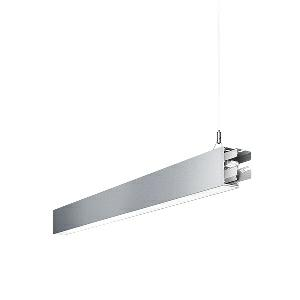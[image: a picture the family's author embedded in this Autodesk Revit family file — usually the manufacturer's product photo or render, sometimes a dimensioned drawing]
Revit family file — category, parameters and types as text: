
# Revit family: idoo_line_-_ilp_4000_vtl_d_mid_00806470_1443
name_source: partatom
category: Lighting Fixtures
units: mm (PartAtom-declared; Revit-internal decimal feet)

## family parameters
Cut with Voids When Loaded = No
Host = Face
Light Source = No
Part Type = Normal
Room Calculation Point = No
Round Connector Dimension = Use Diameter
Shared = No

## types (1)
- IDOO.line - ILP 4000/VTL/D MID (1 x LED, 3850 lm, 2700-6500K)
    Apparent Load = 39 VA
    Approval mark = CE
    CIE Flux Codes = 66 91 98 40 100
    Color Rendering = 90-100
    Color Temperature = 2700-6500K
    Control Gear = Electronic ballast
    Default Elevation = 1800 mm
    Description = ILP 4000/VTL/D|Suspended luminaire|light source: LED|connected load: 220-240 V, 50/60 Hz|Power consumption: approx. 39 W|standby: approx. 0,25|luminous flux: 3850 lm|luminous efficacy: 98 lm/W|light distribution: Direct/indirect|direct ratio: approx. 40 %|colour temperature: Cold white, ca. 2700-6500 K|color rendering index (CRI): >= 90|chromaticity tolerance:  3 SDCM|System of protection: IP 40|technology: Continuously dimmable|luminaire body|material: Sectional aluminium|colour: Silver|lamp cover: Acrylic (PMMA), Clear|mains lead: 1,0 m With free stranded wires|Fastening: Steel cable 0.3 - 0.7 m|glare control: Prism aperture|luminance(L65): <= 2700 cd/m|unified glare rating(4H 8H): <=  16|special features: Specified values at approx. 4000 K, DALI Load 1x, Through-wired, up to 18 m on one mains connection, External control required for Dali Device type 8, Flicker-free, Constant luminous flux between 2700 and 6500 K, Constant colour temperature over the whole dimming range, Suitable as emergency lighting, Mechanical and electrical connection of the individual modules without tools|
    Frequency = 50 Hz
    Height = 110 mm
    Lamp = 1 x LED
    Lamp Light Flux = 3850 lm
    Lamp count = 1
    Length = 1402 mm
    Luminous efficacy = 99 lm/W
    Manufacturer = Waldmann
    ModVariant = No
    Model = 00806470
    Mounting Place = Ceiling
    Mounting Type = Pendant
    Number of Poles = 1
    OnlyDefault = Yes
    Power Factor = 1
    Product Name = IDOO.line - ILP 4000/VTL/D MID
    Product group = Suspended luminaire
    ProductGroupID = 9
    Protection Class = Protection class I
    Protection Degree = IP 40
    RLX_Detail_Level = 1
    RLX_Emergency_Light_Flux = 0 lm
    RLX_Emergency_Type = 0
    RLX_Emergency_Type_DB = No
    RlxData = <blob elided: 22137 chars, md5=832befc8>
    Socket = socket
    Standby Power = 0 W
    System Light Flux = 3850 lm
    System Power = 39 W
    Type Comments = Product without accessories
    Type Image = 113311000-00692597.jpg
    URL = http://relux.com
    VarID = ---
    Voltage = 230 V
    Voltage Range = 220-240 V
    Weight = 0.00 kg
    Width = 60 mm  [stored 0.19685 ft]

note: [stored X ft] marks values corroborated as IEEE doubles in the binary element streams (Revit-internal decimal feet)

## geometry (parser evidence)
native form markers: Blend x4, Sweep x13
no freeform markers — native parametric forms only
